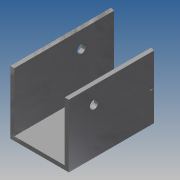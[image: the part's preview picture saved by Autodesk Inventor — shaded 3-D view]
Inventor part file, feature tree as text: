
AUTODESK INVENTOR PART (.ipt)
format: ipt  version: 2014 SP1 (Build 180222100, 222)  size: 134,656 bytes
history: native  units: in
note: dims shown in document units (in); Inventor stores cm internally (conversion verified against a paired STEP export)
features: sketch x5, extrude x3, hole x2, plane x1
ambient origin geometry x8: Origin, YZ Plane, XZ Plane, XY Plane, X Axis, Y Axis, Z Axis, Center Point
bodies: Solid1 (feature_tree)
feature tree (11):
  extrude  "channel"  Depth=1.75in
  extrude  "angleCut"  Depth=0.12in
  hole  "Hole1"  [1 undecoded]
  hole  "Hole2"  [1 undecoded]
  plane  "Work Plane1"
  extrude  "indentMark"  Depth=0.1in
  sketch  "Sketch1"  dims[d0=1.5in d1=1.75in]
  sketch  "Sketch2"  dims[d2=1.75in d3=0.12in]
  sketch  "Sketch3"  dims[d4=3.0in d5=0.0in d6=2.0in]
  sketch  "Sketch5"  dims[d7=15.0deg d8=4.0in d9=0.0in]
  sketch  "Sketch6"  dims[d10=0.75in d11=0.5in d12=0.25in d13=0.75in d14=0.375in d15=0.25in d16=0.5635in d17=1.0in d18=0.8108in d19=2.0in d20=0.5in d21=0.25in d22=0.75in d23=0.375in d24=0.25in d25=0.5635in d26=1.0in d27=0.8108in d28=90.0deg d29=0.1in d30=0.1in d31=4.0in d32=0.0in]
note: 2 required parameter values undecoded (feature->parameter linkage not recoverable at this tier; creation-order binding heuristic only, values carry confidence <= 0.55)
